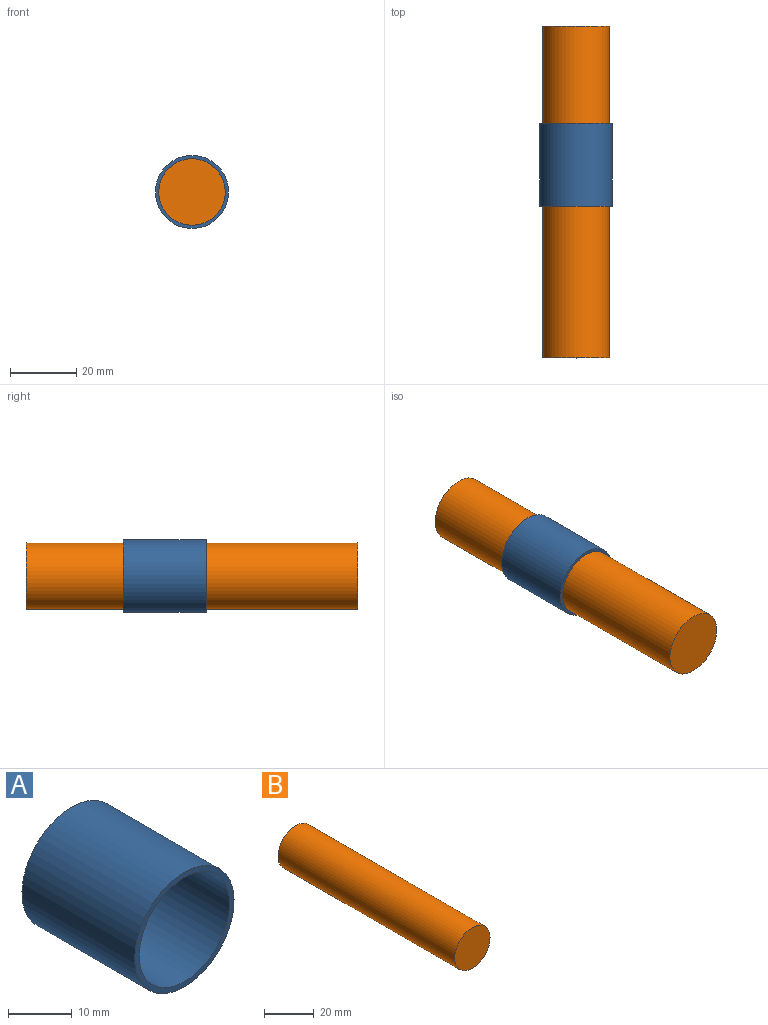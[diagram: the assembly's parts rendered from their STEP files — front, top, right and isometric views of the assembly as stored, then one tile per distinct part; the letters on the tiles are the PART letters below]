
ASSEMBLY  parts=2 mates=1
PART A: 4 faces, bbox 22x25x22 mm
  f0: cylinder r=10mm len=25mm, axis (0,1,0), area 1570.8mm2, adj f2,f3
  f1: cylinder r=11mm len=25mm, axis (0,1,0), area 1727.9mm2, adj f2,f3
  f2: plane 22x22mm, normal (0,-1,0), area 66mm2, adj f0,f1
  f3: plane 22x22mm, normal (0,1,0), area 66mm2, adj f0,f1
PART B: 3 faces, bbox 20x100x20 mm
  f0: cylinder r=10mm len=100mm, axis (0,1,0), area 6283.2mm2, adj f1,f2
  f1: plane 20x20mm, normal (0,-1,0), area 314.2mm2, adj f0
  f2: plane 20x20mm, normal (0,1,0), area 314.2mm2, adj f0
PLACE A t=(-42.54,-29.31,-5.75)mm
PLACE B at identity fixed
MATE slider B.f0 <-> A.f0  axis (0,-1,0) through (-47.85,-100,34.92)mm
